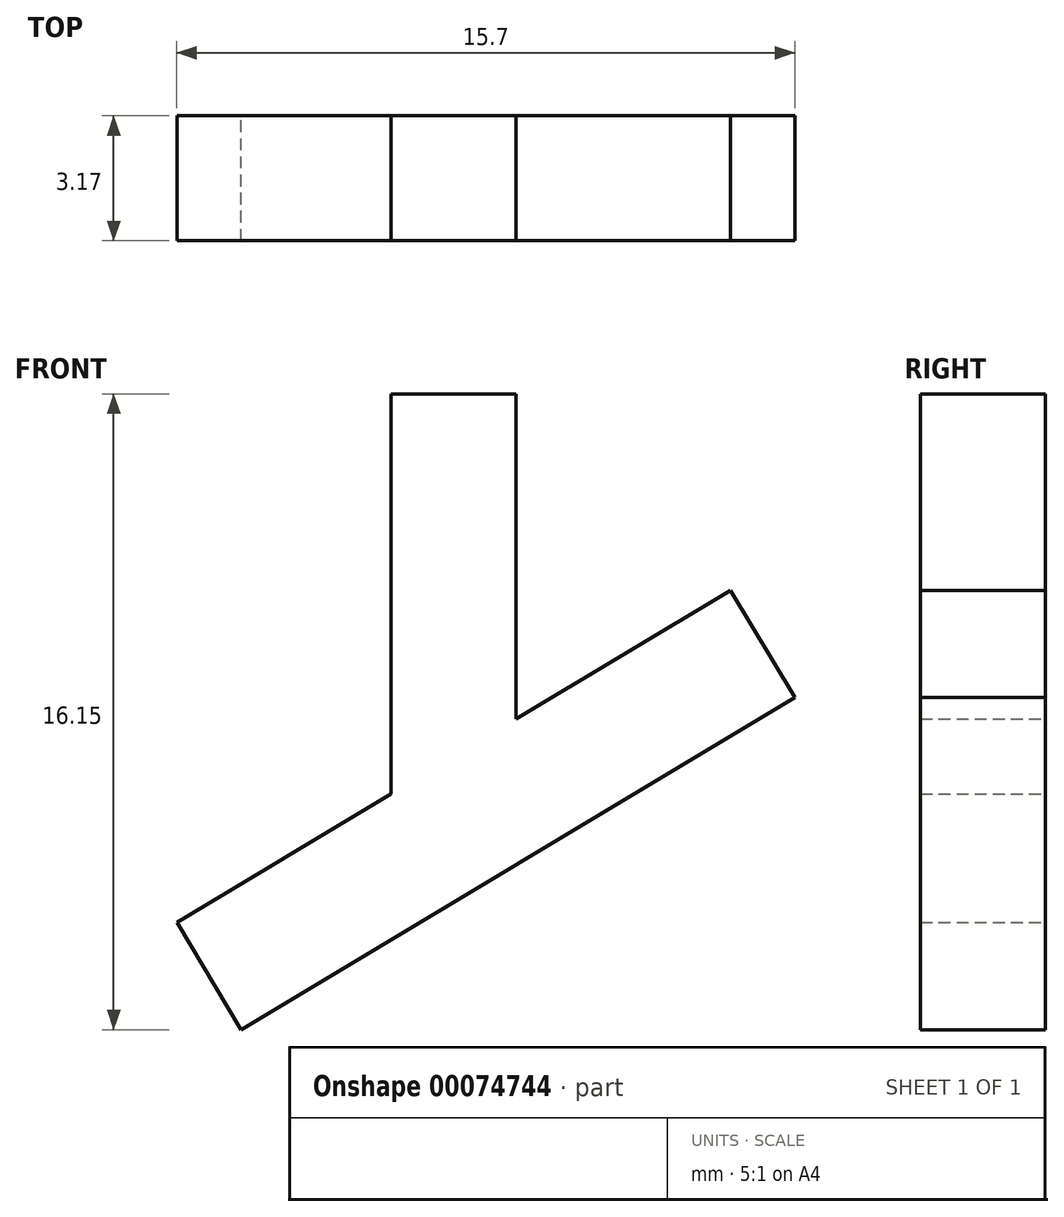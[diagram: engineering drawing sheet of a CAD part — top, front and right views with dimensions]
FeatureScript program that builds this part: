
annotation { "Feature Type Name" : "Feature", "Feature Type Description" : "" }
export const myFeature = defineFeature(function(context is Context, id is Id, definition is map)
    precondition{}
    {
        {
            var Q0;
            Q0=qCreatedBy(makeId("Front.planeOp"),FACE);
            var sketch = newSketch(context, id + "F0", { "sketchPlane" : qUnion([Q0])});
            skLineSegment(sketch, "E0", {"start": v(0, 0) * mm, "end": v(0, -10.16) * mm});
            skLineSegment(sketch, "E1", {"start": v(0, 0) * mm, "end": v(3.18, 0) * mm});
            skLineSegment(sketch, "E2", {"start": v(3.18, 0) * mm, "end": v(3.18, -10.16) * mm});
            skLineSegment(sketch, "E3", {"start": v(0, -10.16) * mm, "end": v(3.18, -10.16) * mm});
            skSolve(sketch);
        }
        {
            var Q0;
            Q0 = qSketchRegion(id + "F0", true);
            extrude(context, id + "F1", {"entities" : qUnion([Q0]), "depth" : 3.17 * mm});
        }
        {
            var Q0;
            Q0=makeQuery(id+"F1.opExtrude","SWEPT_EDGE",EDGE,{"disambiguationData":[OSD([sQuery(id+"F0.wireOp",EDGE,"E2"),sQuery(id+"F0.wireOp",EDGE,"E3")])]});
            chamfer(context, id + "F2", {"entities" : qUnion([Q0]), "chamferType" : ChamferType.TWO_OFFSETS, "width1" : 1.9 * mm, "oppositeDirection" : false, "width2" : 3.17 * mm, "tangentPropagation" : true});
        }
        {
            var Q0;
            Q0=makeQuery(id+"F2.opChamfer","BLEND_FACE",FACE,{"disambiguationData":[OSD([sQuery(id+"F0.wireOp",EDGE,"E2"),sQuery(id+"F0.wireOp",EDGE,"E3")])]});
            extrude(context, id + "F3", {"entities" : qUnion([Q0]), "depth" : 3.17 * mm});
        }
        {
            var Q0;
            Q0=makeQuery(id+"F3.opExtrude","SWEPT_FACE",FACE,{"disambiguationData":[OSD([sQuery(id+"F0.wireOp",EDGE,"E2"),sQuery(id+"F0.wireOp",EDGE,"E3")])]});
            extrude(context, id + "F4", {"entities" : qUnion([Q0]), "operationType" : NewBodyOperationType.ADD, "depth" : 6.35 * mm});
        }
        {
            var Q0;
            Q0=makeQuery(id+"F3.opExtrude","SWEPT_FACE",FACE,{"disambiguationData":[OSD([sQuery(id+"F0.wireOp",EDGE,"E0"),sQuery(id+"F0.wireOp",EDGE,"E2"),sQuery(id+"F0.wireOp",EDGE,"E3")])]});
            extrude(context, id + "F5", {"entities" : qUnion([Q0]), "operationType" : NewBodyOperationType.ADD, "depth" : 6.35 * mm});
        }
    });
